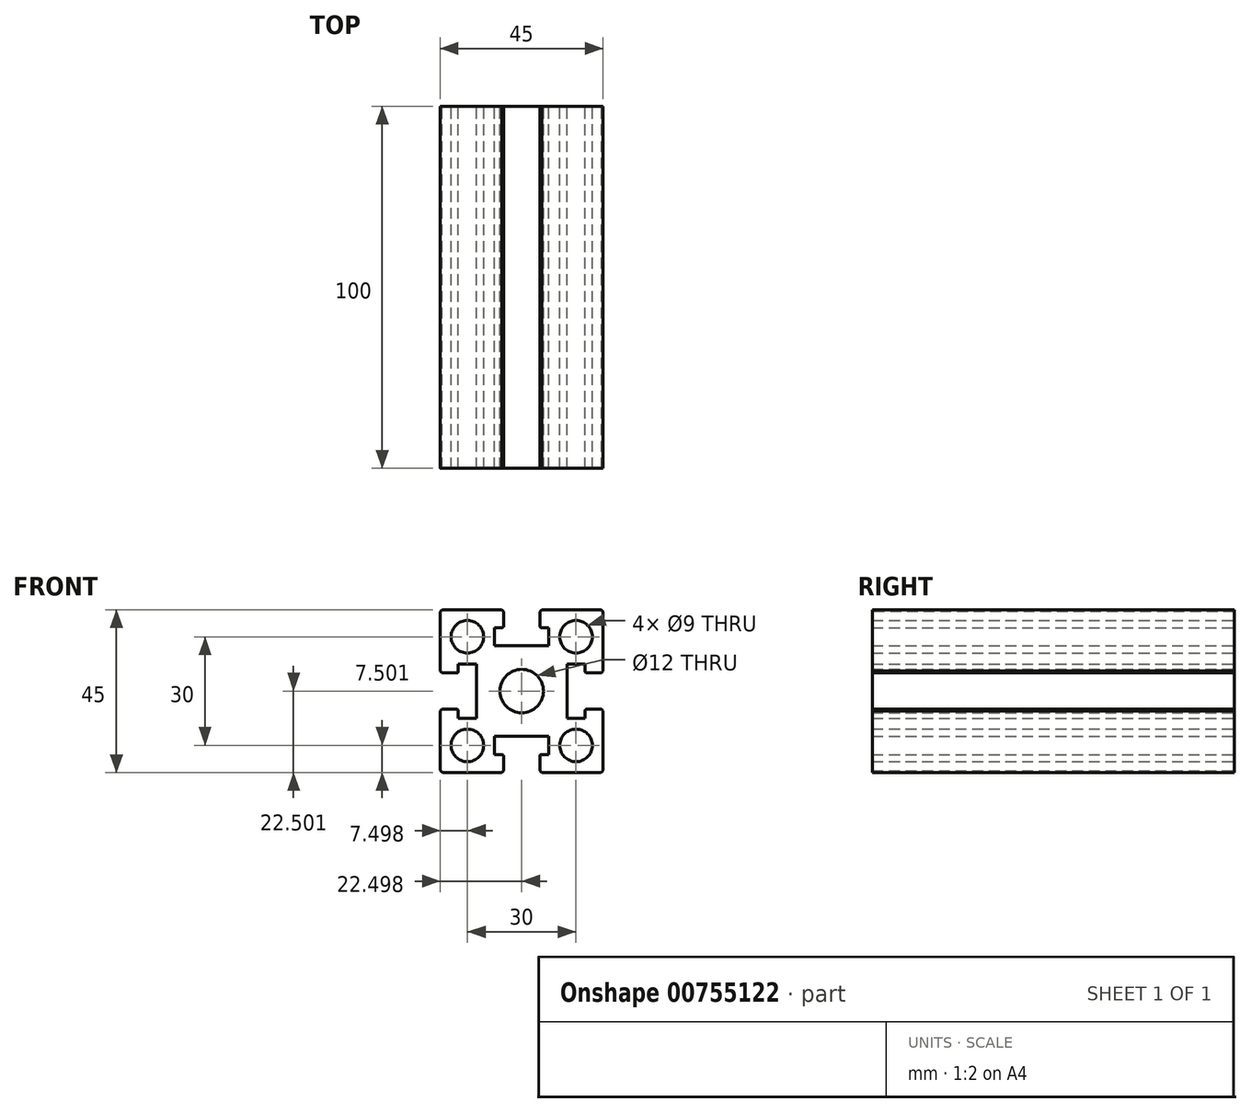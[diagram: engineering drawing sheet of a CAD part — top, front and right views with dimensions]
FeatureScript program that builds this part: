
annotation { "Feature Type Name" : "Feature", "Feature Type Description" : "" }
export const myFeature = defineFeature(function(context is Context, id is Id, definition is map)
    precondition{}
    {
        {
            var Q0;
            Q0=qCreatedBy(makeId("Front.planeOp"),FACE);
            var sketch = newSketch(context, id + "F0", { "sketchPlane" : qUnion([Q0])});
            skLineSegment(sketch, "E0.left", {"start": v(21.62, -21.03) * mm, "end": v(21.62, -3.53) * mm});
            skLineSegment(sketch, "E0.right", {"start": v(-23.38, -21.03) * mm, "end": v(-23.38, -3.53) * mm});
            skPoint(sketch, "E0.middle", {"position": v(-0.88, 1.47) * mm});
            skCircle(sketch, "E1", {"center": v(-0.88, 1.47) * mm, "radius": 6 * mm});
            skLineSegment(sketch, "E2.bottom", {"start": v(-23.38, 6.47) * mm, "end": v(-18.38, 6.47) * mm});
            skLineSegment(sketch, "E2.top", {"start": v(-23.38, -3.53) * mm, "end": v(-18.38, -3.53) * mm});
            skLineSegment(sketch, "E3", {"start": v(-18.38, 6.47) * mm, "end": v(-18.38, 8.97) * mm});
            skLineSegment(sketch, "E4", {"start": v(-18.38, 8.97) * mm, "end": v(-13.38, 8.97) * mm});
            skLineSegment(sketch, "E5", {"start": v(-13.38, 8.97) * mm, "end": v(-13.38, -6.03) * mm});
            skLineSegment(sketch, "E6", {"start": v(-18.38, -3.53) * mm, "end": v(-18.38, -6.03) * mm});
            skLineSegment(sketch, "E7", {"start": v(-18.38, -6.03) * mm, "end": v(-13.38, -6.03) * mm});
            skLineSegment(sketch, "E8.trimOffspring", {"start": v(-23.38, 6.47) * mm, "end": v(-23.38, 23.97) * mm});
            skLineSegment(sketch, "E9.MirrorCS", {"start": v(21.62, -3.53) * mm, "end": v(16.62, -3.53) * mm});
            skLineSegment(sketch, "E10.MirrorCS", {"start": v(16.62, -6.03) * mm, "end": v(11.62, -6.03) * mm});
            skLineSegment(sketch, "E11.MirrorCS", {"start": v(11.62, 8.97) * mm, "end": v(11.62, -6.03) * mm});
            skLineSegment(sketch, "E12.MirrorCS", {"start": v(16.62, 8.97) * mm, "end": v(11.62, 8.97) * mm});
            skLineSegment(sketch, "E13.MirrorCS", {"start": v(21.62, 6.47) * mm, "end": v(16.62, 6.47) * mm});
            skLineSegment(sketch, "E14", {"start": v(16.62, 8.97) * mm, "end": v(16.62, 6.47) * mm});
            skLineSegment(sketch, "E15", {"start": v(16.62, -3.53) * mm, "end": v(16.62, -6.03) * mm});
            skLineSegment(sketch, "E16.trimOffspring", {"start": v(21.62, 6.47) * mm, "end": v(21.62, 23.97) * mm});
            skPoint(sketch, "E17", {"position": v(14.12, -13.53) * mm});
            skPoint(sketch, "E18", {"position": v(14.12, 16.47) * mm});
            skPoint(sketch, "E19", {"position": v(-15.88, 16.47) * mm});
            skPoint(sketch, "E20", {"position": v(-15.88, -13.53) * mm});
            skCircle(sketch, "E21", {"center": v(14.12, -13.53) * mm, "radius": 4.5 * mm});
            skCircle(sketch, "E22", {"center": v(-15.88, -13.53) * mm, "radius": 4.5 * mm});
            skCircle(sketch, "E23", {"center": v(-15.88, 16.47) * mm, "radius": 4.5 * mm});
            skCircle(sketch, "E24", {"center": v(14.12, 16.47) * mm, "radius": 4.5 * mm});
            skLineSegment(sketch, "E25", {"start": v(-23.38, 23.97) * mm, "end": v(-5.88, 23.97) * mm});
            skLineSegment(sketch, "E26", {"start": v(-23.38, -21.03) * mm, "end": v(-5.88, -21.03) * mm});
            skLineSegment(sketch, "E27.left", {"start": v(-5.88, 23.97) * mm, "end": v(-5.88, 18.97) * mm});
            skLineSegment(sketch, "E27.right", {"start": v(4.12, 23.97) * mm, "end": v(4.12, 18.97) * mm});
            skLineSegment(sketch, "E28.bottom", {"start": v(-8.38, 18.97) * mm, "end": v(-5.88, 18.97) * mm});
            skLineSegment(sketch, "E28.top", {"start": v(-8.38, 13.97) * mm, "end": v(6.62, 13.97) * mm});
            skLineSegment(sketch, "E28.left", {"start": v(-8.38, 18.97) * mm, "end": v(-8.38, 13.97) * mm});
            skLineSegment(sketch, "E28.right", {"start": v(6.62, 18.97) * mm, "end": v(6.62, 13.97) * mm});
            skLineSegment(sketch, "E29.trimOffspring", {"start": v(4.12, 23.97) * mm, "end": v(21.62, 23.97) * mm});
            skLineSegment(sketch, "E30.trimOffspring", {"start": v(4.12, 18.97) * mm, "end": v(6.62, 18.97) * mm});
            skLineSegment(sketch, "E31.left", {"start": v(-5.88, -21.03) * mm, "end": v(-5.88, -16.03) * mm});
            skLineSegment(sketch, "E31.right", {"start": v(4.12, -21.03) * mm, "end": v(4.12, -16.03) * mm});
            skLineSegment(sketch, "E32.bottom", {"start": v(-8.38, -11.03) * mm, "end": v(6.62, -11.03) * mm});
            skLineSegment(sketch, "E32.top", {"start": v(-8.38, -16.03) * mm, "end": v(-5.88, -16.03) * mm});
            skLineSegment(sketch, "E32.left", {"start": v(-8.38, -11.03) * mm, "end": v(-8.38, -16.03) * mm});
            skLineSegment(sketch, "E32.right", {"start": v(6.62, -11.03) * mm, "end": v(6.62, -16.03) * mm});
            skLineSegment(sketch, "E33.bottom", {"start": v(6.62, -11.03) * mm, "end": v(6.62, -11.03) * mm});
            skLineSegment(sketch, "E33.top", {"start": v(6.62, -16.03) * mm, "end": v(6.62, -16.03) * mm});
            skLineSegment(sketch, "E34.trimOffspring", {"start": v(4.12, -16.03) * mm, "end": v(6.62, -16.03) * mm});
            skLineSegment(sketch, "E35.trimOffspring", {"start": v(4.12, -21.03) * mm, "end": v(21.62, -21.03) * mm});
            skSolve(sketch);
        }
        {
            var Q0;
            Q0=makeQuery(id+"F0.imprint","IMPRINT",FACE,{"disambiguationData":[TD([[makeQuery(id+"F0.imprint","IMPRINT",EDGE,{"derivedFrom":sQuery(id+"F0.wireOp",EDGE,"E0.left")}),1.0]])]});
            extrude(context, id + "F1", {"entities" : qUnion([Q0]), "depth" : 100 * mm, "offsetDistance" : 25 * mm});
        }
        {
            var Q0;
            Q0=makeQuery(id+"F1.opExtrude","SWEPT_EDGE",EDGE,{"disambiguationData":[OSD([sQuery(id+"F0.wireOp",EDGE,"E16.trimOffspring"),sQuery(id+"F0.wireOp",EDGE,"E29.trimOffspring")])]});
            var Q1;
            Q1=makeQuery(id+"F1.opExtrude","SWEPT_EDGE",EDGE,{"disambiguationData":[OSD([sQuery(id+"F0.wireOp",EDGE,"E0.left"),sQuery(id+"F0.wireOp",EDGE,"E35.trimOffspring")])]});
            var Q2;
            Q2=makeQuery(id+"F1.opExtrude","SWEPT_EDGE",EDGE,{"disambiguationData":[OSD([sQuery(id+"F0.wireOp",EDGE,"E0.right"),sQuery(id+"F0.wireOp",EDGE,"E26")])]});
            var Q3;
            Q3=makeQuery(id+"F1.opExtrude","SWEPT_EDGE",EDGE,{"disambiguationData":[OSD([sQuery(id+"F0.wireOp",EDGE,"E8.trimOffspring"),sQuery(id+"F0.wireOp",EDGE,"E25")])]});
            fillet(context, id + "F2", {"entities" : qUnion([Q0, Q1, Q2, Q3]), "radius" : 1 * mm, "tangentPropagation" : true, "allowEdgeOverflow" : false});
        }
        {
            var Q0;
            Q0=makeQuery(id+"F1.opExtrude","SWEPT_EDGE",EDGE,{"disambiguationData":[OSD([sQuery(id+"F0.wireOp",EDGE,"E31.right"),sQuery(id+"F0.wireOp",EDGE,"E34.trimOffspring")])]});
            var Q1;
            Q1=makeQuery(id+"F1.opExtrude","SWEPT_EDGE",EDGE,{"disambiguationData":[OSD([sQuery(id+"F0.wireOp",EDGE,"E13.MirrorCS"),sQuery(id+"F0.wireOp",EDGE,"E14")])]});
            var Q2;
            Q2=makeQuery(id+"F1.opExtrude","SWEPT_EDGE",EDGE,{"disambiguationData":[OSD([sQuery(id+"F0.wireOp",EDGE,"E9.MirrorCS"),sQuery(id+"F0.wireOp",EDGE,"E15")])]});
            var Q3;
            Q3=makeQuery(id+"F1.opExtrude","SWEPT_EDGE",EDGE,{"disambiguationData":[OSD([sQuery(id+"F0.wireOp",EDGE,"E27.right"),sQuery(id+"F0.wireOp",EDGE,"E30.trimOffspring")])]});
            var Q4;
            Q4=makeQuery(id+"F1.opExtrude","SWEPT_EDGE",EDGE,{"disambiguationData":[OSD([sQuery(id+"F0.wireOp",EDGE,"E27.left"),sQuery(id+"F0.wireOp",EDGE,"E28.bottom")])]});
            var Q5;
            Q5=makeQuery(id+"F1.opExtrude","SWEPT_EDGE",EDGE,{"disambiguationData":[OSD([sQuery(id+"F0.wireOp",EDGE,"E2.bottom"),sQuery(id+"F0.wireOp",EDGE,"E3")])]});
            var Q6;
            Q6=makeQuery(id+"F1.opExtrude","SWEPT_EDGE",EDGE,{"disambiguationData":[OSD([sQuery(id+"F0.wireOp",EDGE,"E2.top"),sQuery(id+"F0.wireOp",EDGE,"E6")])]});
            var Q7;
            Q7=makeQuery(id+"F1.opExtrude","SWEPT_EDGE",EDGE,{"disambiguationData":[OSD([sQuery(id+"F0.wireOp",EDGE,"E31.left"),sQuery(id+"F0.wireOp",EDGE,"E32.top")])]});
            fillet(context, id + "F3", {"entities" : qUnion([Q0, Q1, Q2, Q3, Q4, Q5, Q6, Q7]), "radius" : .5 * mm, "tangentPropagation" : true, "allowEdgeOverflow" : false});
        }
        {
            var Q0;
            Q0=makeQuery(id+"F1.opExtrude","SWEPT_EDGE",EDGE,{"disambiguationData":[OSD([sQuery(id+"F0.wireOp",EDGE,"E0.right"),sQuery(id+"F0.wireOp",EDGE,"E2.top")])]});
            var Q1;
            Q1=makeQuery(id+"F1.opExtrude","SWEPT_EDGE",EDGE,{"disambiguationData":[OSD([sQuery(id+"F0.wireOp",EDGE,"E2.bottom"),sQuery(id+"F0.wireOp",EDGE,"E8.trimOffspring")])]});
            var Q2;
            Q2=makeQuery(id+"F1.opExtrude","SWEPT_EDGE",EDGE,{"disambiguationData":[OSD([sQuery(id+"F0.wireOp",EDGE,"E25"),sQuery(id+"F0.wireOp",EDGE,"E27.left")])]});
            var Q3;
            Q3=makeQuery(id+"F1.opExtrude","SWEPT_EDGE",EDGE,{"disambiguationData":[OSD([sQuery(id+"F0.wireOp",EDGE,"E27.right"),sQuery(id+"F0.wireOp",EDGE,"E29.trimOffspring")])]});
            var Q4;
            Q4=makeQuery(id+"F1.opExtrude","SWEPT_EDGE",EDGE,{"disambiguationData":[OSD([sQuery(id+"F0.wireOp",EDGE,"E0.left"),sQuery(id+"F0.wireOp",EDGE,"E9.MirrorCS")])]});
            var Q5;
            Q5=makeQuery(id+"F1.opExtrude","SWEPT_EDGE",EDGE,{"disambiguationData":[OSD([sQuery(id+"F0.wireOp",EDGE,"E31.right"),sQuery(id+"F0.wireOp",EDGE,"E35.trimOffspring")])]});
            var Q6;
            Q6=makeQuery(id+"F1.opExtrude","SWEPT_EDGE",EDGE,{"disambiguationData":[OSD([sQuery(id+"F0.wireOp",EDGE,"E13.MirrorCS"),sQuery(id+"F0.wireOp",EDGE,"E16.trimOffspring")])]});
            var Q7;
            Q7=makeQuery(id+"F1.opExtrude","SWEPT_EDGE",EDGE,{"disambiguationData":[OSD([sQuery(id+"F0.wireOp",EDGE,"E26"),sQuery(id+"F0.wireOp",EDGE,"E31.left")])]});
            chamfer(context, id + "F4", {"entities" : qUnion([Q0, Q1, Q2, Q3, Q4, Q5, Q6, Q7]), "width" : .5 * mm, "tangentPropagation" : true});
        }
    });
